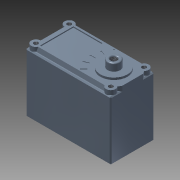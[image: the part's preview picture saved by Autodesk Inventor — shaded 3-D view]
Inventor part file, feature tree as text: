
AUTODESK INVENTOR PART (.ipt)
format: ipt  version: 2013 (Build 170138000, 138)  size: 360,448 bytes
history: native  units: mm
features: sketch x15, extrude x10, hole x5, thread x5, chamfer x4, pattern_circular x2, other x1, fillet x1
ambient origin geometry x1: Origin
feature tree (43):
  other  "ソリッド1"
  extrude  "押し出し1"  Depth=21.0mm
  hole  "穴1"  [1 undecoded]
  extrude  "押し出し2"  Depth=41.0mm
  extrude  "押し出し3"  Depth=20.5mm
  hole  "穴2"  [1 undecoded]
  extrude  "押し出し4"  Depth=2.0mm
  pattern_circular  "円形状パターン1"  [2 undecoded]
  extrude  "押し出し5"  Depth=36.0mm
  chamfer  "面取り1"  Distance=16.0mm
  chamfer  "面取り2"  Distance=16.0mm
  chamfer  "面取り3"  Distance=2.5mm
  extrude  "押し出し6"  Depth=2.5mm
  hole  "穴3"  [1 undecoded]
  extrude  "押し出し7"  Depth=2.5mm
  extrude  "押し出し8"  Depth=13.0mm
  hole  "穴4"  [1 undecoded]
  extrude  "押し出し9"  Depth=10.5mm
  pattern_circular  "円形状パターン2"  [2 undecoded]
  extrude  "押し出し10"  Depth=6.0mm
  chamfer  "面取り5"  Distance=3.5mm
  fillet  "フィレット2"  Radius=3.0mm
  thread  "ねじ1"
  thread  "ねじ2"
  thread  "ねじ3"
  thread  "ねじ4"
  thread  "ねじ5"
  hole  "穴5"  [1 undecoded]
  sketch  "スケッチ1"
  sketch  "スケッチ2"
  sketch  "スケッチ3"
  sketch  "スケッチ4"
  sketch  "スケッチ5"
  sketch  "スケッチ6"
  sketch  "スケッチ8"
  sketch  "スケッチ10"
  sketch  "スケッチ12"
  sketch  "スケッチ13"
  sketch  "スケッチ14"
  sketch  "スケッチ15"
  sketch  "スケッチ16"
  sketch  "スケッチ18"
  sketch  "スケッチ19"
note: 9 required parameter values undecoded (feature->parameter linkage not recoverable at this tier; creation-order binding heuristic only, values carry confidence <= 0.55)
